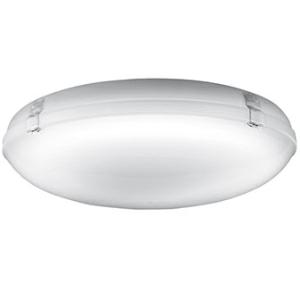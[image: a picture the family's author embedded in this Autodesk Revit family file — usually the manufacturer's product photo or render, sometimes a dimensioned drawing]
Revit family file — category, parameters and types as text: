
# Revit family: 3f_filippi_-_3f_petra_sensor_3f_filippi_-_34334_-_3f_petra_op_380_22w_led_sensor
name_source: partatom
category: Lighting Fixtures
units: mm (PartAtom-declared; Revit-internal decimal feet)

## family parameters
Cut with Voids When Loaded = No
Host = Face
Light Source = No
Part Type = Normal
Room Calculation Point = No
Round Connector Dimension = Use Diameter
Shared = No

## types (1)
- 3F Filippi - 3F Petra Sensor (1 x LED, 2978 lm, 26 W, 4000 K)
    Apparent Load = 26 VA
    Approval mark = ENEC
    CIE Flux Codes = 43 73 91 90 100
    Color Rendering = 80
    Color Temperature = 4000 K
    Control Gear = Electronic ballast
    Default Elevation = 1800 mm
    Description = ILLUMINOTECHNICAL
Luminous efficiency 100% (DLOR 90%, ULOR 10%).
Initial luminous flux of the luminaire 2978 lm.
Diffused symmetric distribution.
Installation Interdistance Transv.D = 1.26 x hu - Long.D = 1.25 x hu.
Tabular UGR (CIE 117 - 4H-8H; S=0.25H; 70/50/20): RUG 21.3 - 21.2.
Beam angle: 117° - 116°.
Luminous efficacy 115 lm/W.
Lifetime (L93/B10): 30000 h. (tq+25°C)
Lifetime (L90/B10): 50000 h. (tq+25°C)
Lifetime (L85/B10): 80000 h. (tq+25°C)
Lifetime (L80/B10): 100000 h. (tq+25°C)
Sudden decreased luminous flux after 50000 hours: 0% (C0).
Photobiological safety in compliance with IEC/TR 62778: RG0 risk exempt, (IEC 62471).
In compliance with IEC/EN 62722-2-1 - IEC/EN 62717 standards.

SOURCE
Circular LED module 22W/840.
Energy efficiency class (UE 2019/2020 - UE 2019/2015): C.
CIE 13.3 Colour rendering index: CRI >80 (R9 <50%).
IES TM-30 Fidelity Index: Rf = 84 Rg = 95.
CCT nominal colour temperature 4000 K.
Colour initial tolerance (MacAdam): SDCM 3.

MECHANICAL
Housing in glazed self-extinguishing V2 polycarbonate, UV stabilised, injection moulded.
Ecologic anti-aging injected sealing gasket.
Gear-tray reflector unit in aluminium, painted in white epoxy-polyester, fixed to the housing by quick-fastening steel devices, hinged opening.
Diffuser in opal methacrylate (PMMA), injection moulded.
Snug fit safety snap-lock clips for diffuser mounting in transparent polycarbonate, screwdriver opening.
Luminaire with limited surface temperature. - D - (EN 60598-2-24)
Dimensions: diameter 380 mm, height 117 mm. Weight 1.725 kg.
IP64 protection degree.
Mechanical strength to impacts IK02 (0.2 joule).
Glow-wire test resistance 650°C.

ELECTRICAL
Halogen Free electronic wiring 230V-50/60Hz, power factor 0.70, THD <25%, constant output current, SELV, class I, 1 driver.
High frequency radar motion sensor, integrated in the luminarie.
Power of the luminaire 26 W.
CE - IEC 60598-1 - EN 60598-1.
SAFE FLICKER: PstLM=<1 and SVM=<0.4 (IEC TR 61547-1 and IEC TR 63158), to ensure a more comfortable and safe light.
Ambient temperature from 0°C to +25°C.
Temperature class T6 max 85°C.
Relative humidity UR: <85%.

INSTALLATION
Ceiling / Wall.

APPLICATIONS
Suitable product for food production plants (HACCP), IFS (Food Version 6), BRC (GSFS Food Version 7).
Transit areas, stairwells. Environments where a diffused lighting provides visual comfort.
Virtually in all environments compatibly with the emissions/atmospheres compromising the use of plastic materials.
Not suitable for installation on surfaces subject to important vibrations, exposed to weather conditions.

LIGHT MANAGEMENT
The radar movement sensor, integrated in the device, allows switching on/off as a result of presence detection and the set twilight threshold.
Recommended installation height on ceiling up to 4 m and on wall up to 2.7 m.

WARNING
Luminaire designed for disposal/recycling at end-of-life.
Replaceable (LED only) light source by a professional. Replaceable control gear by a professional.
    Height = 117 mm
    Lamp = 1 x LED
    Lamp Light Flux = 2978 lm
    Lamp Power = 26 W
    Lamp count = 1
    Length = 380 mm
    Lifetime = 50000 h
    Luminous efficacy = 115 lm/W
    Manufacturer = 3F Filippi
    ModVariant = No
    Model = 3F Filippi - 34334 - 3F Petra OP 380 22W LED Sensor
    Mounting Place = Ceiling
    Mounting Type = Surface mounted
    Number of Poles = 1
    OnlyDefault = Yes
    Power Factor = 1
    Product Name = 3F Filippi - 3F Petra Sensor
    Product group = ceiling mounted luminaire
    ProductGroupID = 3
    Protection Class = Protection class I
    Protection Degree = IP 64
    RLX_Detail_Level = 1
    RLX_Emergency_Light_Flux = 0 lm
    RLX_Emergency_Type = 0
    RLX_Emergency_Type_DB = No
    RlxData = <blob elided: 225001 chars, md5=0a03534d>
    Socket = socket
    Standby Power = 0 W
    System Light Flux = 2978 lm
    System Power = 26 W
    Type Comments = Product without accessories
    Type Image = 3ffilippi_34334.jpg
    URL = http://relux.com
    VarID = ---
    Voltage = 0 V
    Weight = 0.00 kg
    Width = 0 mm  [stored 0 ft]

note: [stored X ft] marks values corroborated as IEEE doubles in the binary element streams (Revit-internal decimal feet)

## geometry (parser evidence)
native form markers: Blend x4, Sweep x12
no freeform markers — native parametric forms only
